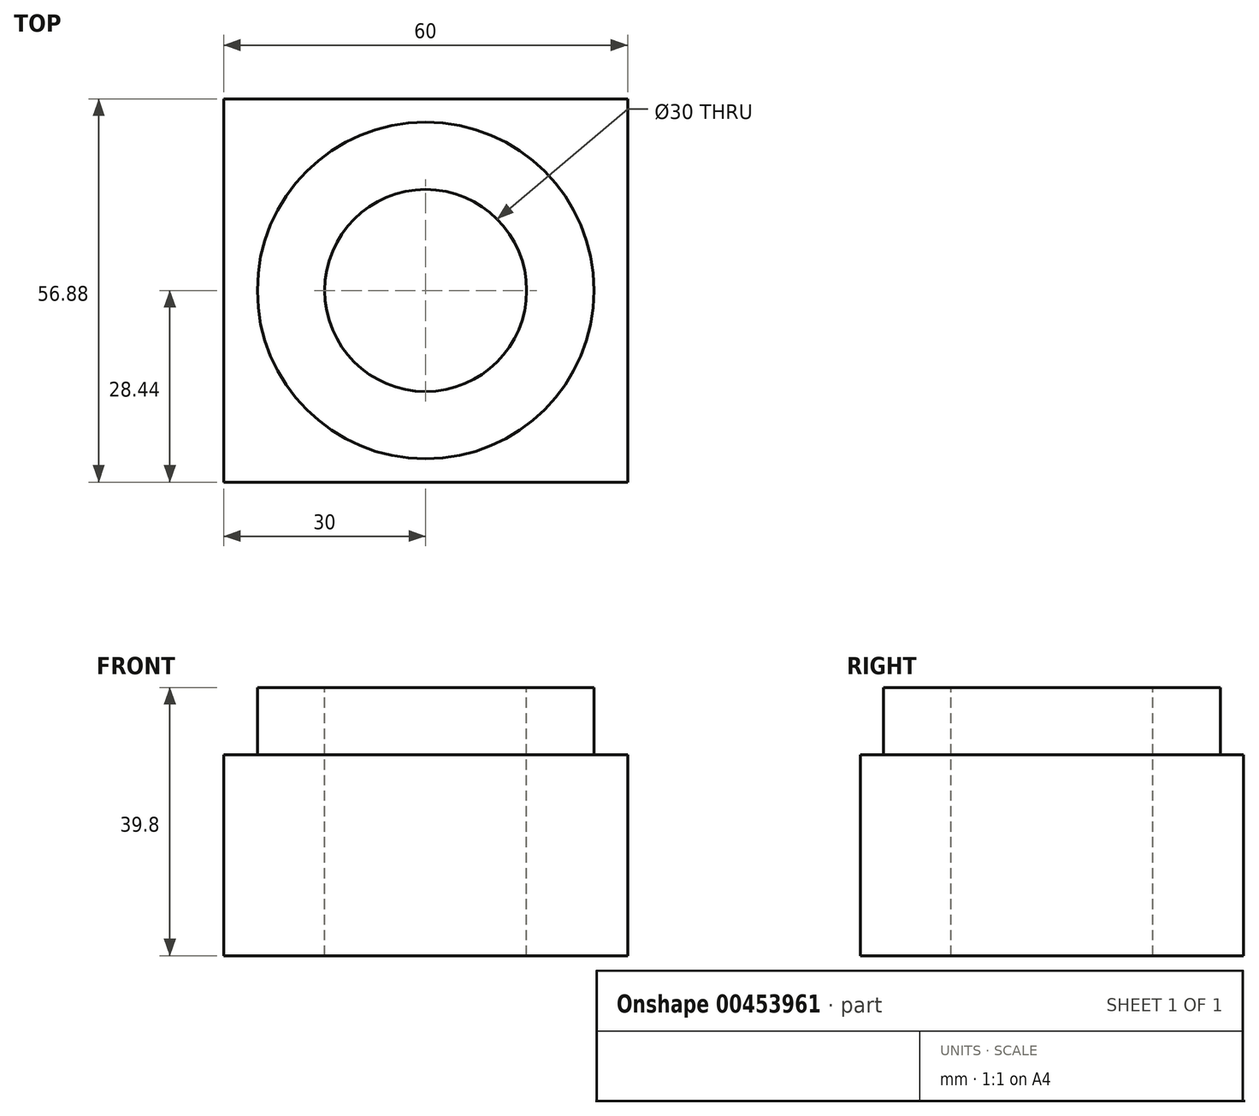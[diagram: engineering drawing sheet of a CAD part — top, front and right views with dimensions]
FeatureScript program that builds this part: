
annotation { "Feature Type Name" : "Feature", "Feature Type Description" : "" }
export const myFeature = defineFeature(function(context is Context, id is Id, definition is map)
    precondition{}
    {
        {
            var Q0;
            Q0=qCreatedBy(makeId("Top.planeOp"),FACE);
            var sketch = newSketch(context, id + "F0", { "sketchPlane" : qUnion([Q0])});
            skCircle(sketch, "E0", {"center": v(0, 0) * mm, "radius": 25 * mm});
            skSolve(sketch);
        }
        {
            var Q0;
            Q0 = qSketchRegion(id + "F0", true);
            extrude(context, id + "F1", {"entities" : qUnion([Q0]), "depth" : 10 * mm});
        }
        {
            var Q0;
            Q0=qCreatedBy(makeId("Top.planeOp"),FACE);
            var sketch = newSketch(context, id + "F2", { "sketchPlane" : qUnion([Q0])});
            skLineSegment(sketch, "E1.bottom", {"start": v(-30, 28.44) * mm, "end": v(30, 28.44) * mm});
            skLineSegment(sketch, "E1.top", {"start": v(-30, -28.44) * mm, "end": v(30, -28.44) * mm});
            skLineSegment(sketch, "E1.left", {"start": v(-30, 28.44) * mm, "end": v(-30, -28.44) * mm});
            skLineSegment(sketch, "E1.right", {"start": v(30, 28.44) * mm, "end": v(30, -28.44) * mm});
            skPoint(sketch, "E1.middle", {"position": v(0, 0) * mm});
            skSolve(sketch);
        }
        {
            var Q0;
            Q0 = qSketchRegion(id + "F2", true);
            var Q1;
            Q1=makeQuery(id+"F1.opExtrude","CAP_FACE",FACE,{"disambiguationData":[OSD([sQuery(id+"F0.wireOp",EDGE,"E0")])],"isStart":false});
            extrude(context, id + "F3", {"entities" : qUnion([Q0, Q1]), "operationType" : NewBodyOperationType.ADD, "oppositeDirection" : true, "depth" : 29.8 * mm});
        }
        {
            var Q0;
            Q0=makeQuery(id+"F1.opExtrude","CAP_FACE",FACE,{"disambiguationData":[OSD([sQuery(id+"F0.wireOp",EDGE,"E0")])],"isStart":false});
            var sketch = newSketch(context, id + "F4", { "sketchPlane" : qUnion([Q0])});
            skCircle(sketch, "E2", {"center": v(0, 0) * mm, "radius": 15 * mm});
            skSolve(sketch);
        }
        {
            var Q0;
            Q0=makeQuery(id+"F4.imprint","IMPRINT",FACE,{"disambiguationData":[TD([[makeQuery(id+"F4.imprint","IMPRINT",EDGE,{"derivedFrom":sQuery(id+"F4.wireOp",EDGE,"E2")}),1.0]])]});
            extrude(context, id + "F5", {"entities" : qUnion([Q0]), "operationType" : NewBodyOperationType.REMOVE, "oppositeDirection" : true, "depth" : 47.7 * mm});
        }
    });
